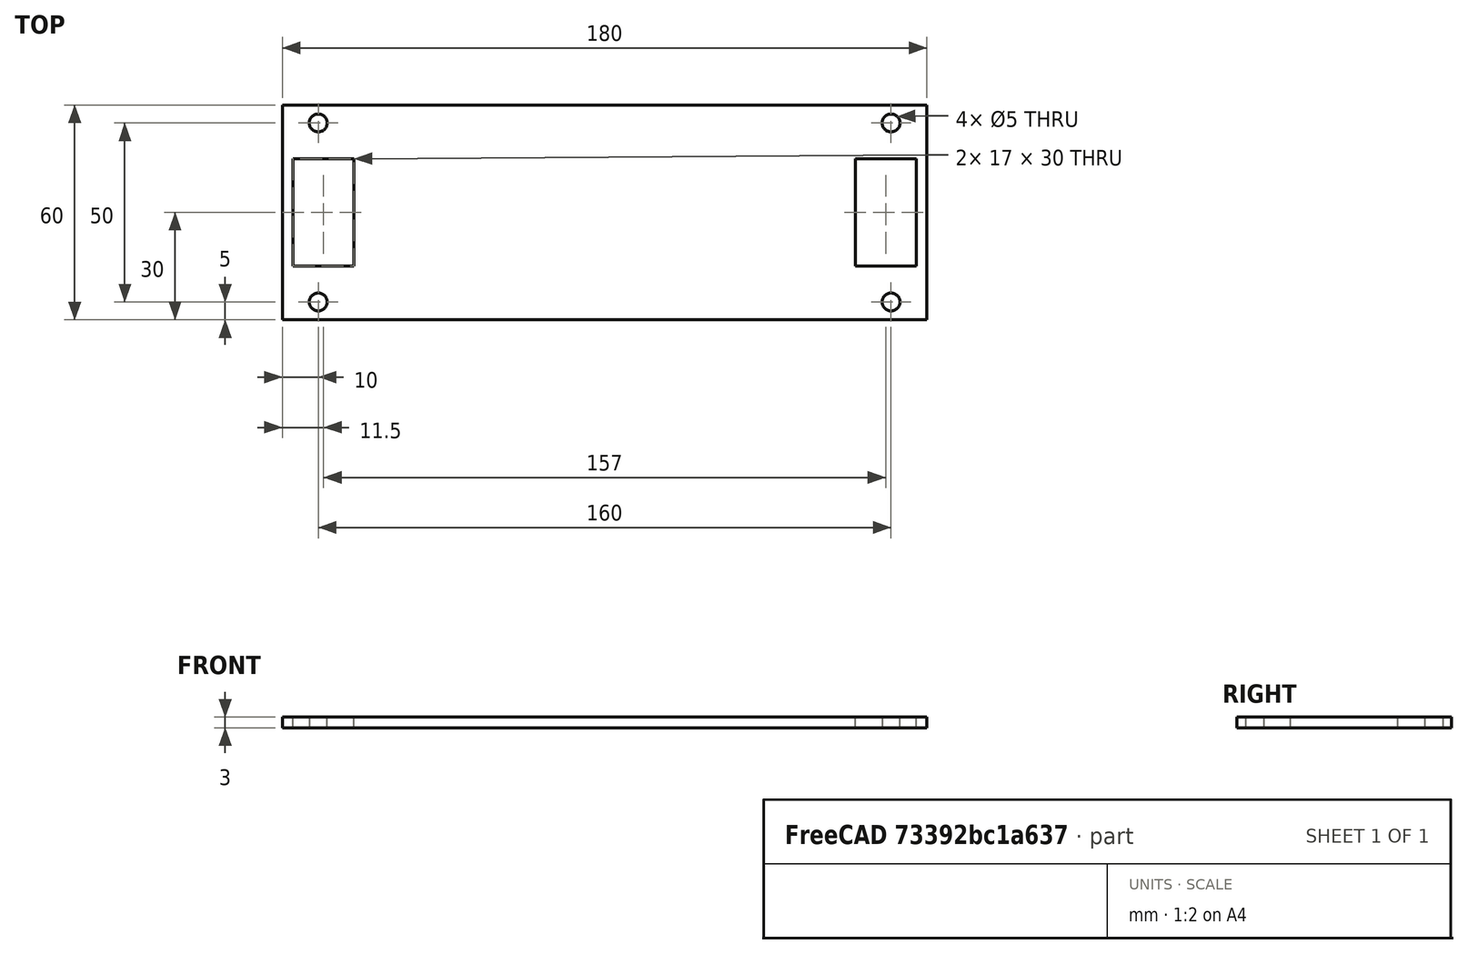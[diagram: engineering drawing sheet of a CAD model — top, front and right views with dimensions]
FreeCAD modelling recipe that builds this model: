
FCSTD DOCUMENT  (FreeCAD 0.16R6707 (Git))
Label: support haut tiges
License: All rights reserved
LicenseURL: http://en.wikipedia.org/wiki/All_rights_reserved
objects: Sketcher::SketchObject×1, PartDesign::Pad×1
note: 3 computed .brp shape members not serialized (recipe doc carries the construction recipe); baked Part::Feature solids carry a one-line shape summary decoded from their .brp

FEATURE [Sketcher::SketchObject] Sketch
  sketch-geometry (22):
    g0: LineSegment StartX=0 StartY=0 StartZ=0 EndX=180 EndY=0 EndZ=0
    g1: LineSegment StartX=180 StartY=0 StartZ=0 EndX=180 EndY=60 EndZ=0
    g2: LineSegment StartX=180 StartY=60 StartZ=0 EndX=0 EndY=60 EndZ=0
    g3: LineSegment StartX=0 StartY=60 StartZ=0 EndX=0 EndY=0 EndZ=0
    g4: GeomPoint [constr] X=10 Y=5 Z=0
    g5: GeomPoint [constr] X=10 Y=55 Z=0
    g6: GeomPoint [constr] X=170 Y=5 Z=0
    g7: GeomPoint [constr] X=170 Y=55 Z=0
    g8: Circle CenterX=10 CenterY=55 CenterZ=0 NormalX=0 NormalY=0 NormalZ=1 Radius=2.5
    g9: Circle CenterX=170 CenterY=55 CenterZ=0 NormalX=0 NormalY=0 NormalZ=1 Radius=2.5
    g10: Circle CenterX=170 CenterY=5 CenterZ=0 NormalX=0 NormalY=0 NormalZ=1 Radius=2.5
    g11: Circle CenterX=10 CenterY=5 CenterZ=0 NormalX=0 NormalY=0 NormalZ=1 Radius=2.5
    g12: GeomPoint [constr] X=20 Y=15 Z=0
    g13: GeomPoint [constr] X=160 Y=15 Z=0
    g14: LineSegment StartX=20 StartY=15 StartZ=0 EndX=3 EndY=15 EndZ=0
    g15: LineSegment StartX=3 StartY=15 StartZ=0 EndX=3 EndY=45 EndZ=0
    g16: LineSegment StartX=3 StartY=45 StartZ=0 EndX=20 EndY=45 EndZ=0
    g17: LineSegment StartX=20 StartY=45 StartZ=0 EndX=20 EndY=15 EndZ=0
    g18: LineSegment StartX=160 StartY=15 StartZ=0 EndX=177 EndY=15 EndZ=0
    g19: LineSegment StartX=177 StartY=15 StartZ=0 EndX=177 EndY=45 EndZ=0
    g20: LineSegment StartX=177 StartY=45 StartZ=0 EndX=160 EndY=45 EndZ=0
    g21: LineSegment StartX=160 StartY=45 StartZ=0 EndX=160 EndY=15 EndZ=0
  constraints (53):
    c: Coincident(g0,g1)
    c: Coincident(g1,g2)
    c: Coincident(g2,g3)
    c: Coincident(g3,g0)
    c: Horizontal(g0)
    c: Horizontal(g2)
    c: Vertical(g1)
    c: Vertical(g3)
    c: Coincident(g0,g-1)
    c: Distance(g3) = 60
    c: Distance(g2) = 180
    c: DistanceX(g4) = 10
    c: DistanceY(g4) = 5
    c: DistanceX(g4,g5) = 0
    c: DistanceY(g4,g5) = 50
    c: DistanceX(g6) = 170
    c: DistanceY(g4,g6) = 0
    c: DistanceY(g6,g7) = 50
    c: DistanceX(g7,g6) = 0
    c: Coincident(g8,g5)
    c: Coincident(g9,g7)
    c: Coincident(g10,g6)
    c: Coincident(g11,g4)
    c: Radius(g11) = 2.5
    c: Radius(g8) = 2.5
    c: Radius(g9) = 2.5
    c: Radius(g10) = 2.5
    c: DistanceY(g4,g12) = 10
    c: DistanceX(g4,g12) = 10
    c: Coincident(g14,g15)
    c: Coincident(g15,g16)
    c: Coincident(g16,g17)
    c: Coincident(g17,g14)
    c: Horizontal(g14)
    c: Horizontal(g16)
    c: Vertical(g15)
    c: Vertical(g17)
    c: Coincident(g14,g12)
    c: Distance(g17) = 30
    c: Distance(g16) = 17
    c: DistanceY(g12,g13) = 0
    c: DistanceX(g13,g6) = 10
    c: Coincident(g18,g19)
    c: Coincident(g19,g20)
    c: Coincident(g20,g21)
    c: Coincident(g21,g18)
    c: Horizontal(g18)
    c: Horizontal(g20)
    c: Vertical(g19)
    c: Vertical(g21)
    c: Coincident(g18,g13)
    c: Distance(g20) = 17
    c: Distance(g21) = 30
FEATURE [PartDesign::Pad] Pad
  Length = 3
  Length2 = 100
  Sketch = -> Sketch
  Type = 0
